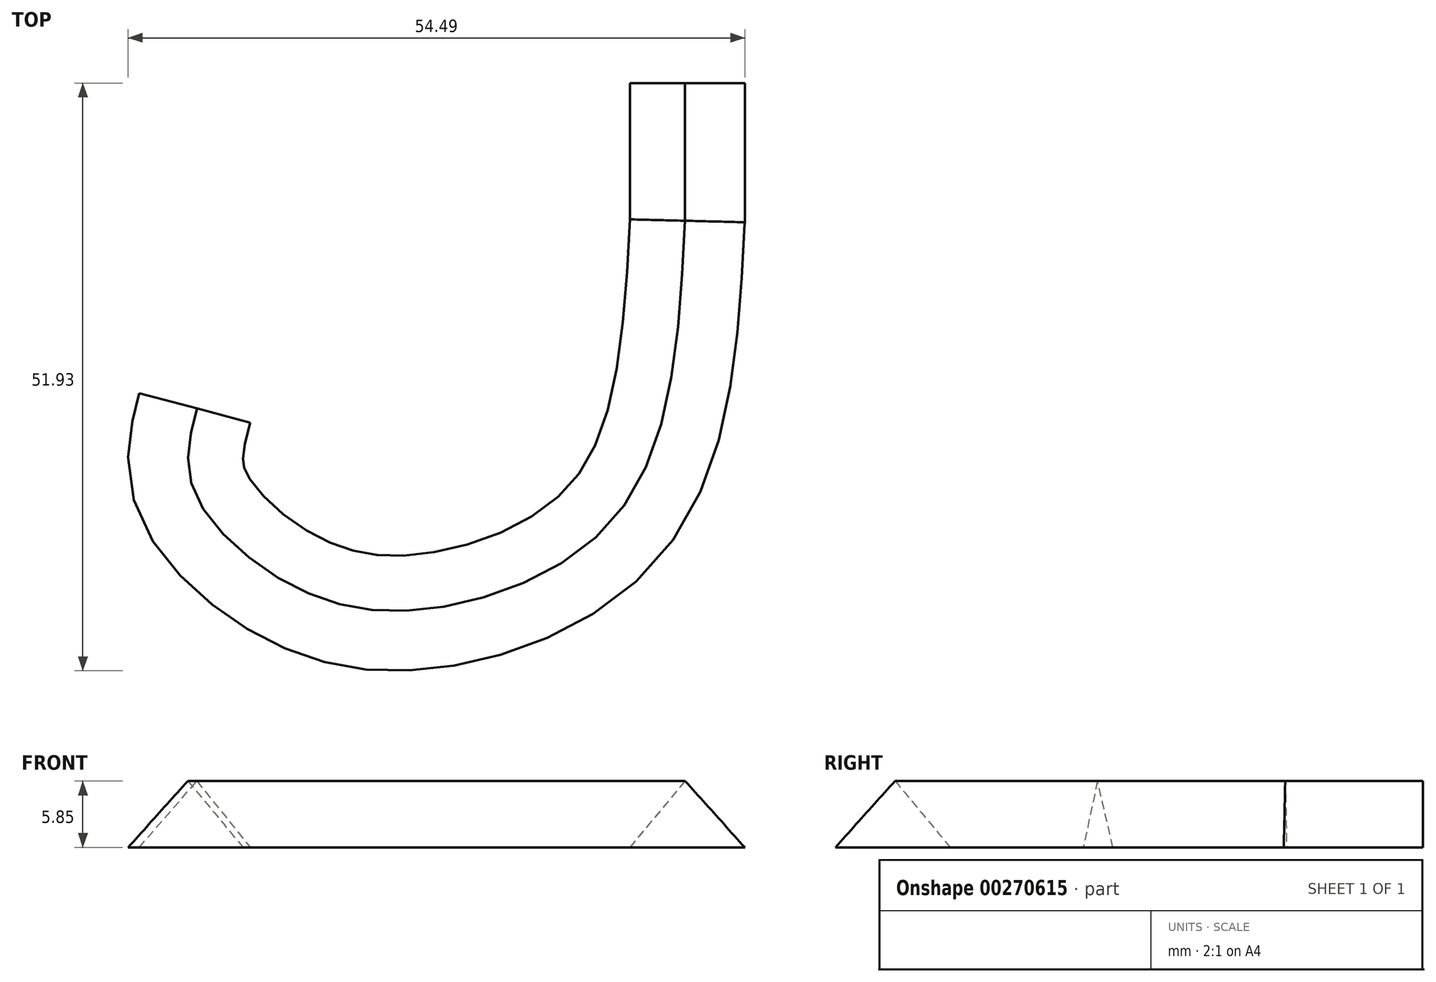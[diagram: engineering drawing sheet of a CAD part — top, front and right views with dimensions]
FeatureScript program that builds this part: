
annotation { "Feature Type Name" : "Feature", "Feature Type Description" : "" }
export const myFeature = defineFeature(function(context is Context, id is Id, definition is map)
    precondition{}
    {
        {
            var Q0;
            Q0=qCreatedBy(makeId("Front.planeOp"),FACE);
            var sketch = newSketch(context, id + "F0", { "sketchPlane" : qUnion([Q0])});
            skLineSegment(sketch, "E0", {"start": v(0, 5.85) * mm, "end": v(-4.88, 0) * mm});
            skLineSegment(sketch, "E1", {"start": v(-4.88, 0) * mm, "end": v(5.28, 0) * mm});
            skLineSegment(sketch, "E2", {"start": v(5.28, 0) * mm, "end": v(0, 5.85) * mm});
            skSolve(sketch);
        }
        {
            var Q0;
            Q0=qCreatedBy(makeId("Top.planeOp"),FACE);
            var sketch = newSketch(context, id + "F1", { "sketchPlane" : qUnion([Q0])});
            skLineSegment(sketch, "E3", {"start": v(0, 0) * mm, "end": v(0, -12.17) * mm});
            skFitSpline(sketch, "E4", {"points": [v(0, -12.17) * mm, v(-5.72, -37.8) * mm, v(-22.68, -46.46) * mm, v(-35.03, -44.25) * mm, v(-43.5, -35.76) * mm, v(-43.14, -28.76) * mm], "startDerivative": vector(-5.47, -108.98) * mm, "endDerivative": vector(13.33, 49.9) * mm});
            skSolve(sketch);
        }
        {
            var Q0;
            Q0 = qSketchRegion(id + "F0", true);
            var Q1;
            Q1=sQuery(id+"F1.wireOp",EDGE,"E4");
            var Q2;
            Q2=sQuery(id+"F1.wireOp",EDGE,"E3");
            sweep(context, id + "F2", {"profiles" : qUnion([Q0]), "path" : qUnion([Q1, Q2])});
        }
    });
